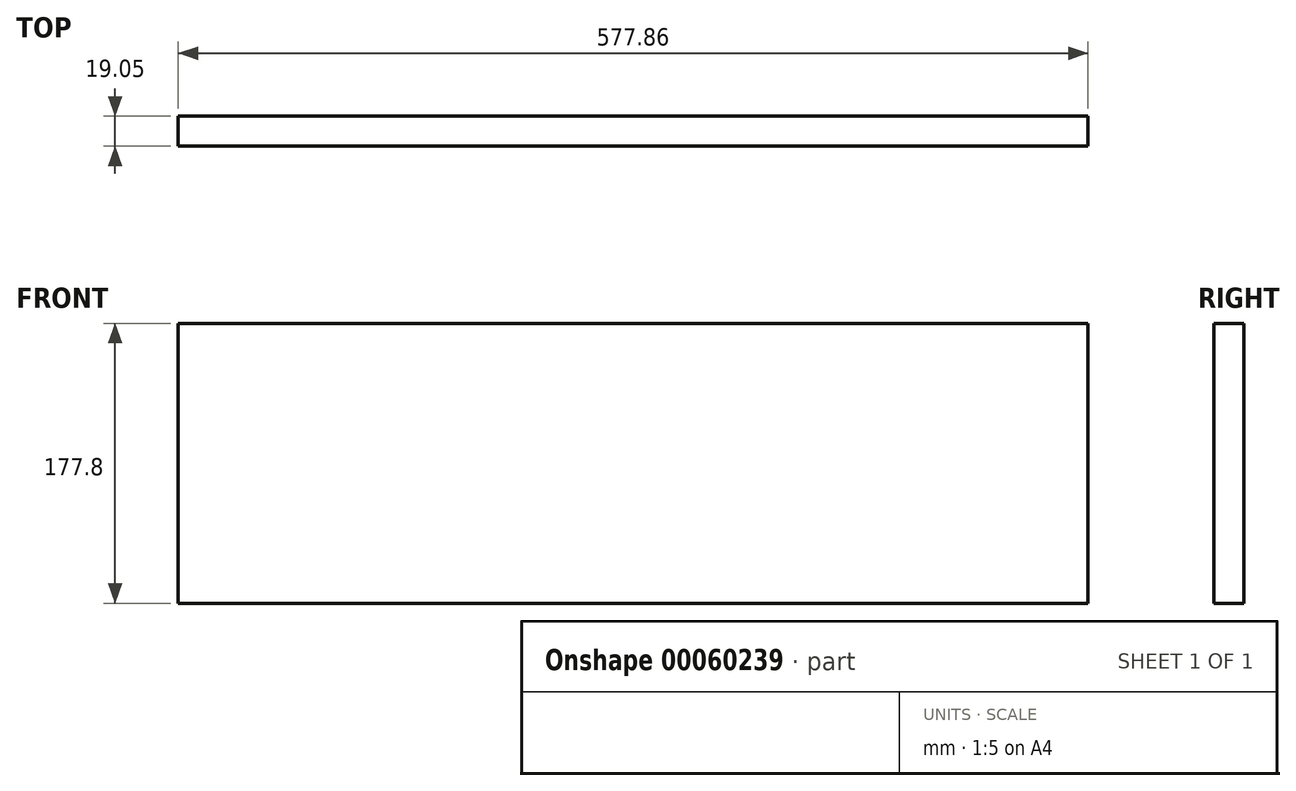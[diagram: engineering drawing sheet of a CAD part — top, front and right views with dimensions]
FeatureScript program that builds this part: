
annotation { "Feature Type Name" : "Feature", "Feature Type Description" : "" }
export const myFeature = defineFeature(function(context is Context, id is Id, definition is map)
    precondition{}
    {
        {
            var Q0;
            Q0=qCreatedBy(makeId("Front.planeOp"),FACE);
            var sketch = newSketch(context, id + "F0", { "sketchPlane" : qUnion([Q0])});
            skLineSegment(sketch, "E0.rect.bottom", {"start": v(288.93, -88.9) * mm, "end": v(-288.93, -88.9) * mm});
            skLineSegment(sketch, "E0.rect.top", {"start": v(288.93, 88.9) * mm, "end": v(-288.93, 88.9) * mm});
            skLineSegment(sketch, "E0.rect.left", {"start": v(288.93, -88.9) * mm, "end": v(288.93, 88.9) * mm});
            skLineSegment(sketch, "E0.rect.right", {"start": v(-288.93, -88.9) * mm, "end": v(-288.93, 88.9) * mm});
            skPoint(sketch, "E0.rect.middle", {"position": v(0, 0) * mm});
            skSolve(sketch);
        }
        {
            var Q0;
            Q0=qSketchRegion(id+"F0",true);
            extrude(context, id + "F1", {"entities" : qUnion([Q0]), "depth" : 19.05 * mm});
        }
    });
